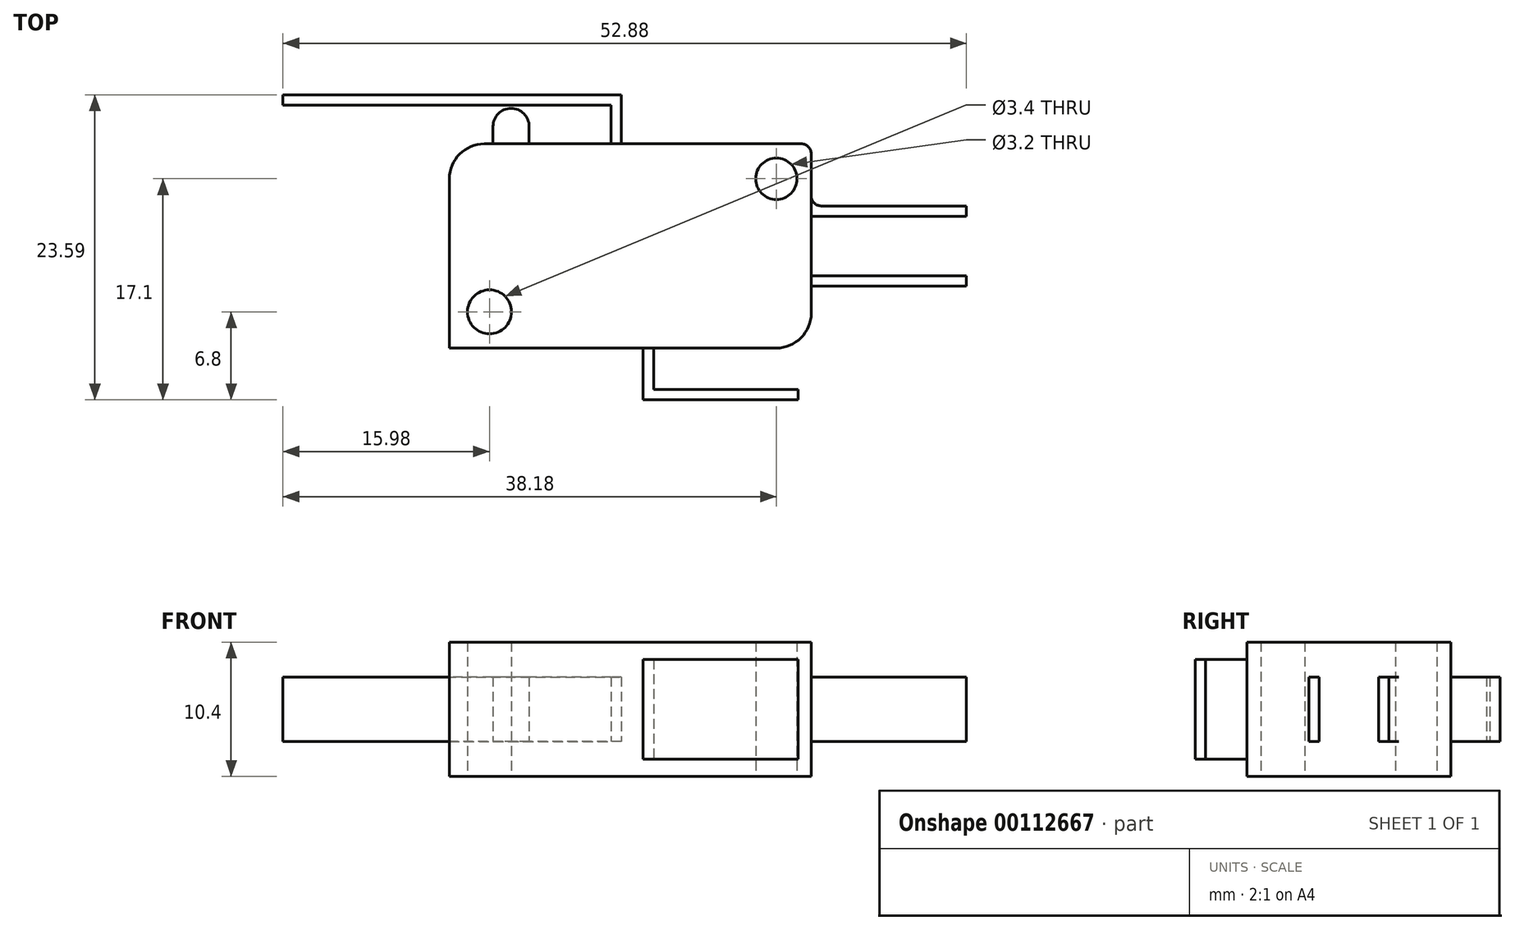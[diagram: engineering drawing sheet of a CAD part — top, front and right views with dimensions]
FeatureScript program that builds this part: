
annotation { "Feature Type Name" : "Feature", "Feature Type Description" : "" }
export const myFeature = defineFeature(function(context is Context, id is Id, definition is map)
    precondition{}
    {
        {
            var Q0;
            Q0=qCreatedBy(makeId("Top.planeOp"),FACE);
            var sketch = newSketch(context, id + "F0", { "sketchPlane" : qUnion([Q0])});
            skLineSegment(sketch, "E0.left", {"start": v(0, 0) * mm, "end": v(0, -15.8) * mm});
            skLineSegment(sketch, "E1", {"start": v(25.3, 0) * mm, "end": v(25.3, -2.7) * mm, "construction": true});
            skLineSegment(sketch, "E2", {"start": v(25.3, -2.7) * mm, "end": v(28, -2.7) * mm, "construction": true});
            skLineSegment(sketch, "E3", {"start": v(3.1, -15.8) * mm, "end": v(3.1, -13) * mm, "construction": true});
            skLineSegment(sketch, "E4", {"start": v(3.1, -13) * mm, "end": v(0, -13) * mm, "construction": true});
            skCircle(sketch, "E5", {"center": v(3.1, -13) * mm, "radius": 1.7 * mm});
            skCircle(sketch, "E6", {"center": v(25.3, -2.7) * mm, "radius": 1.6 * mm});
            skLineSegment(sketch, "E7", {"start": v(0, -15.8) * mm, "end": v(15, -15.8) * mm});
            skLineSegment(sketch, "E8", {"start": v(15, -15.8) * mm, "end": v(15, -19.8) * mm});
            skLineSegment(sketch, "E9", {"start": v(15, -15.8) * mm, "end": v(15.8, -15.8) * mm, "construction": true});
            skLineSegment(sketch, "E10", {"start": v(15.8, -15.8) * mm, "end": v(15.8, -19) * mm});
            skLineSegment(sketch, "E11", {"start": v(15.8, -19) * mm, "end": v(27, -19) * mm});
            skLineSegment(sketch, "E12", {"start": v(27, -19) * mm, "end": v(27, -19.8) * mm});
            skLineSegment(sketch, "E13", {"start": v(27, -19.8) * mm, "end": v(15, -19.8) * mm});
            skLineSegment(sketch, "E14", {"start": v(15.8, -15.8) * mm, "end": v(28, -15.8) * mm});
            skLineSegment(sketch, "E15", {"start": v(28, 0) * mm, "end": v(28, -4.8) * mm});
            skLineSegment(sketch, "E16", {"start": v(28, -15.8) * mm, "end": v(28, -11) * mm});
            skLineSegment(sketch, "E17.bottom", {"start": v(28, -4.8) * mm, "end": v(40, -4.8) * mm});
            skLineSegment(sketch, "E17.top", {"start": v(28, -5.6) * mm, "end": v(40, -5.6) * mm});
            skLineSegment(sketch, "E17.left", {"start": v(28, -4.8) * mm, "end": v(28, -5.6) * mm, "construction": true});
            skLineSegment(sketch, "E17.right", {"start": v(40, -4.8) * mm, "end": v(40, -5.6) * mm});
            skLineSegment(sketch, "E18.bottom", {"start": v(28, -11) * mm, "end": v(40, -11) * mm});
            skLineSegment(sketch, "E18.top", {"start": v(28, -10.2) * mm, "end": v(40, -10.2) * mm});
            skLineSegment(sketch, "E18.left", {"start": v(28, -11) * mm, "end": v(28, -10.2) * mm, "construction": true});
            skLineSegment(sketch, "E18.right", {"start": v(40, -11) * mm, "end": v(40, -10.2) * mm});
            skLineSegment(sketch, "E19", {"start": v(28, -10.2) * mm, "end": v(28, -5.6) * mm});
            skLineSegment(sketch, "E20", {"start": v(0, 0) * mm, "end": v(3.38, 0) * mm});
            skLineSegment(sketch, "E21.bottom", {"start": v(3.38, 0) * mm, "end": v(6.17, 0) * mm, "construction": true});
            skLineSegment(sketch, "E21.top", {"start": v(3.38, 1.35) * mm, "end": v(6.17, 1.35) * mm, "construction": true});
            skLineSegment(sketch, "E21.left", {"start": v(3.38, 0) * mm, "end": v(3.38, 1.35) * mm});
            skLineSegment(sketch, "E21.right", {"start": v(6.17, 0) * mm, "end": v(6.17, 1.35) * mm});
            skArc(sketch, "E22", {"start": v(6.17, 1.35) * mm, "mid": v(4.78, 2.74) * mm, "end": v(3.38, 1.35) * mm});
            skLineSegment(sketch, "E23", {"start": v(6.17, 0) * mm, "end": v(12.52, 0) * mm});
            skLineSegment(sketch, "E24", {"start": v(12.52, 0) * mm, "end": v(12.52, 3) * mm});
            skLineSegment(sketch, "E25", {"start": v(12.52, 3) * mm, "end": v(-12.88, 3) * mm});
            skLineSegment(sketch, "E26", {"start": v(-12.88, 3) * mm, "end": v(-12.88, 3.79) * mm});
            skLineSegment(sketch, "E27", {"start": v(-12.88, 3.79) * mm, "end": v(13.32, 3.79) * mm});
            skLineSegment(sketch, "E28", {"start": v(13.32, 3.79) * mm, "end": v(13.32, 0) * mm});
            skLineSegment(sketch, "E29", {"start": v(12.52, 0) * mm, "end": v(13.32, 0) * mm, "construction": true});
            skLineSegment(sketch, "E30", {"start": v(13.32, 0) * mm, "end": v(28, 0) * mm});
            skSolve(sketch);
        }
        {
            var Q0;
            Q0=makeQuery(id+"F0.imprint","IMPRINT",FACE,{"disambiguationData":[TD([[makeQuery(id+"F0.imprint","IMPRINT",EDGE,{"derivedFrom":sQuery(id+"F0.wireOp",EDGE,"E0.bottom")}),-1.0]])]});
            var Q1;
            Q1=makeQuery(id+"F0.imprint","IMPRINT",FACE,{"disambiguationData":[TD([[makeQuery(id+"F0.imprint","IMPRINT",EDGE,{"derivedFrom":sQuery(id+"F0.wireOp",EDGE,"E0.left")}),1.0]])]});
            extrude(context, id + "F1", {"entities" : qUnion([Q0, Q1]), "depth" : 10.4 * mm});
        }
        {
            var Q0;
            Q0=makeQuery(id+"F1.opExtrude","SWEPT_FACE",FACE,{"disambiguationData":[OSD([sQuery(id+"F0.wireOp",EDGE,"E0.left")])]});
            var sketch = newSketch(context, id + "F2", { "sketchPlane" : qUnion([Q0])});
            skLineSegment(sketch, "E31.bottom", {"start": v(0, 10.4) * mm, "end": v(-12.7, 10.4) * mm});
            skLineSegment(sketch, "E31.top", {"start": v(0, 7.7) * mm, "end": v(-12.7, 7.7) * mm});
            skLineSegment(sketch, "E31.left", {"start": v(0, 10.4) * mm, "end": v(0, 7.7) * mm});
            skLineSegment(sketch, "E31.right", {"start": v(-12.7, 10.4) * mm, "end": v(-12.7, 7.7) * mm});
            skLineSegment(sketch, "E32.bottom", {"start": v(-12.7, 0) * mm, "end": v(0, 0) * mm});
            skLineSegment(sketch, "E32.top", {"start": v(-12.7, 2.7) * mm, "end": v(0, 2.7) * mm});
            skLineSegment(sketch, "E32.left", {"start": v(-12.7, 0) * mm, "end": v(-12.7, 2.7) * mm});
            skLineSegment(sketch, "E32.right", {"start": v(0, 0) * mm, "end": v(0, 2.7) * mm});
            skLineSegment(sketch, "E33.bottom", {"start": v(15.8, 10.4) * mm, "end": v(19.8, 10.4) * mm});
            skLineSegment(sketch, "E33.top", {"start": v(15.8, 9.05) * mm, "end": v(19.8, 9.05) * mm});
            skLineSegment(sketch, "E33.left", {"start": v(15.8, 10.4) * mm, "end": v(15.8, 9.05) * mm});
            skLineSegment(sketch, "E33.right", {"start": v(19.8, 10.4) * mm, "end": v(19.8, 9.05) * mm});
            skLineSegment(sketch, "E34.bottom", {"start": v(15.8, 0) * mm, "end": v(19.8, 0) * mm});
            skLineSegment(sketch, "E34.top", {"start": v(15.8, 1.35) * mm, "end": v(19.8, 1.35) * mm});
            skLineSegment(sketch, "E34.left", {"start": v(15.8, 0) * mm, "end": v(15.8, 1.35) * mm});
            skLineSegment(sketch, "E34.right", {"start": v(19.8, 0) * mm, "end": v(19.8, 1.35) * mm});
            skSolve(sketch);
        }
        {
            var Q0;
            Q0=qSketchRegion(id+"F2",true);
            var Q1;
            Q1=makeQuery(id+"F1.opExtrude","SWEPT_FACE",FACE,{"disambiguationData":[OSD([sQuery(id+"F0.wireOp",EDGE,"E15")])]});
            var Q2;
            Q2=makeQuery(id+"F1.opExtrude","SWEPT_FACE",FACE,{"disambiguationData":[OSD([sQuery(id+"F0.wireOp",EDGE,"E26")])]});
            extrude(context, id + "F3", {"entities" : qUnion([Q0]), "operationType" : NewBodyOperationType.REMOVE, "endBound" : BoundingType.UP_TO_SURFACE, "oppositeDirection" : true, "endBoundEntityFace" : qUnion([Q1]), "depth" : 25.4 * mm, "hasSecondDirection" : true, "secondDirectionBound" : SecondDirectionBoundingType.UP_TO_SURFACE, "secondDirectionOppositeDirection" : false, "secondDirectionBoundEntityFace" : qUnion([Q2]), "secondDirectionDepth" : 25.4 * mm});
        }
        {
            var Q0;
            Q0=makeQuery(id+"F1.opExtrude","SWEPT_FACE",FACE,{"disambiguationData":[OSD([sQuery(id+"F0.wireOp",EDGE,"E17.bottom")])]});
            var sketch = newSketch(context, id + "F4", { "sketchPlane" : qUnion([Q0])});
            skLineSegment(sketch, "E35.bottom", {"start": v(-28, 10.4) * mm, "end": v(-40, 10.4) * mm});
            skLineSegment(sketch, "E35.top", {"start": v(-28, 7.7) * mm, "end": v(-40, 7.7) * mm});
            skLineSegment(sketch, "E35.left", {"start": v(-28, 10.4) * mm, "end": v(-28, 7.7) * mm});
            skLineSegment(sketch, "E35.right", {"start": v(-40, 10.4) * mm, "end": v(-40, 7.7) * mm});
            skLineSegment(sketch, "E36.bottom", {"start": v(-40, 0) * mm, "end": v(-28, 0) * mm});
            skLineSegment(sketch, "E36.top", {"start": v(-40, 2.7) * mm, "end": v(-28, 2.7) * mm});
            skLineSegment(sketch, "E36.left", {"start": v(-40, 0) * mm, "end": v(-40, 2.7) * mm});
            skLineSegment(sketch, "E36.right", {"start": v(-28, 0) * mm, "end": v(-28, 2.7) * mm});
            skSolve(sketch);
        }
        {
            var Q0;
            Q0=qSketchRegion(id+"F4",true);
            var Q1;
            Q1=makeQuery(id+"F1.opExtrude","SWEPT_FACE",FACE,{"disambiguationData":[OSD([sQuery(id+"F0.wireOp",EDGE,"E18.bottom")])]});
            extrude(context, id + "F5", {"entities" : qUnion([Q0]), "operationType" : NewBodyOperationType.REMOVE, "endBound" : BoundingType.UP_TO_SURFACE, "oppositeDirection" : true, "endBoundEntityFace" : qUnion([Q1]), "depth" : 25.4 * mm});
        }
        {
            var Q0;
            Q0=makeQuery(id+"F1.opExtrude","SWEPT_EDGE",EDGE,{"disambiguationData":[OSD([sQuery(id+"F0.wireOp",EDGE,"E14"),sQuery(id+"F0.wireOp",EDGE,"E16")])]});
            var Q1;
            Q1=makeQuery(id+"F3.boolean.opBoolean","INTERSECT",EDGE,{"derivedFrom":[makeQuery(id+"F3.opExtrude","SWEPT_FACE",FACE,{"disambiguationData":[OSD([sQuery(id+"F2.wireOp",EDGE,"E31.left")])]}),makeQuery(id+"F3.opExtrude","SWEPT_FACE",FACE,{"disambiguationData":[OSD([sQuery(id+"F2.wireOp",EDGE,"E32.right")])]})]});
            fillet(context, id + "F6", {"entities" : qUnion([Q0, Q1]), "radius" : 2.7 * mm, "tangentPropagation" : true, "allowEdgeOverflow" : false});
        }
        {
            var Q0;
            Q0=makeQuery(id+"F1.opExtrude","SWEPT_EDGE",EDGE,{"disambiguationData":[OSD([sQuery(id+"F0.wireOp",EDGE,"E15"),sQuery(id+"F0.wireOp",EDGE,"UOBZ1Yfv-CQcf-6u5B-sraZ-4BTIaMxsuPow")])]});
            var Q1;
            Q1=makeQuery(id+"F1.opExtrude","SWEPT_EDGE",EDGE,{"disambiguationData":[OSD([sQuery(id+"F0.wireOp",EDGE,"E0.left"),sQuery(id+"F0.wireOp",EDGE,"E7")])]});
            fillet(context, id + "F7", {"entities" : qUnion([Q0, Q1]), "radius" : 0.76 * mm, "tangentPropagation" : true, "allowEdgeOverflow" : false});
        }
    });
